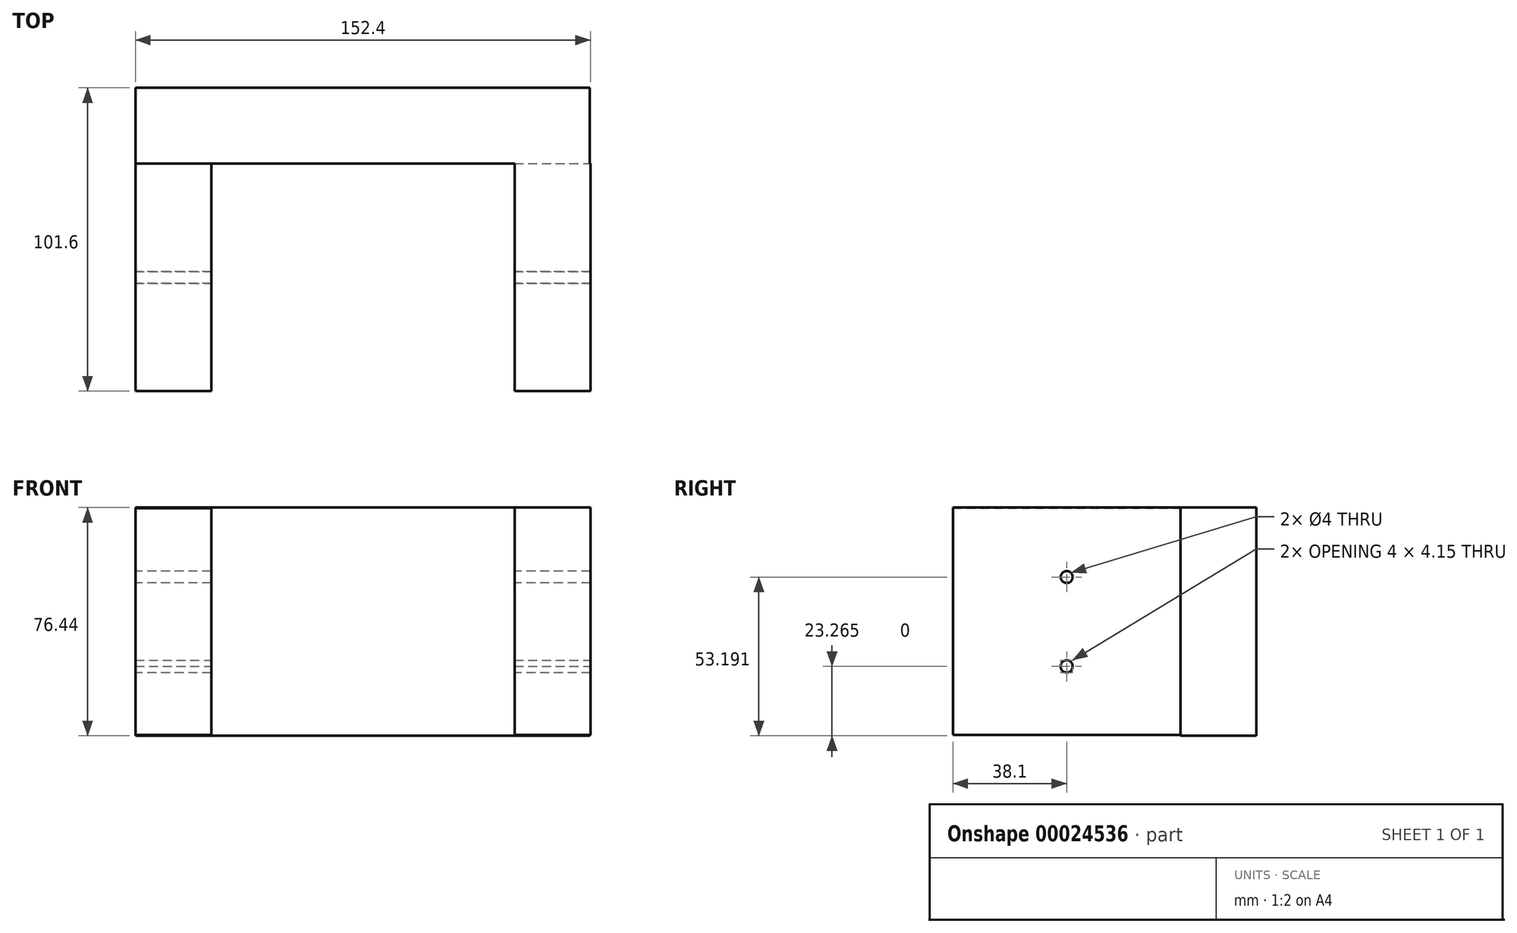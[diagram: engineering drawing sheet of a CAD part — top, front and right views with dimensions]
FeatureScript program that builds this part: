
annotation { "Feature Type Name" : "Feature", "Feature Type Description" : "" }
export const myFeature = defineFeature(function(context is Context, id is Id, definition is map)
    precondition{}
    {
        {
            var Q0;
            Q0=qCreatedBy(makeId("Front.planeOp"),FACE);
            var sketch = newSketch(context, id + "F0", { "sketchPlane" : qUnion([Q0])});
            skLineSegment(sketch, "E0.bottom", {"start": v(0, 0) * mm, "end": v(152.4, 0) * mm});
            skLineSegment(sketch, "E0.top", {"start": v(0, -76.2) * mm, "end": v(152.4, -76.2) * mm});
            skLineSegment(sketch, "E0.left", {"start": v(0, 0) * mm, "end": v(0, -76.2) * mm});
            skLineSegment(sketch, "E0.right", {"start": v(152.4, 0) * mm, "end": v(152.4, -76.2) * mm});
            skLineSegment(sketch, "E1", {"start": v(0, -0.15) * mm, "end": v(25.4, -0.15) * mm});
            skLineSegment(sketch, "E2", {"start": v(152.4, 0.15) * mm, "end": v(127, 0.15) * mm});
            skLineSegment(sketch, "E3", {"start": v(25.4, -0.15) * mm, "end": v(25.4, -76.2) * mm});
            skLineSegment(sketch, "E4", {"start": v(25.4, -76.2) * mm, "end": v(0, -76.2) * mm});
            skLineSegment(sketch, "E5", {"start": v(127, 0.15) * mm, "end": v(127, -76.2) * mm});
            skLineSegment(sketch, "E6", {"start": v(127, -76.2) * mm, "end": v(152.4, -76.2) * mm});
            skSolve(sketch);
        }
        {
            var Q0;
            {var subQ1=sQuery(id+"F0.wireOp",EDGE,"E1");Q0=makeQuery(id+"F0.imprint","IMPRINT",FACE,{"disambiguationData":[TD([[makeQuery(id+"F0.imprint","IMPRINT",EDGE,{"derivedFrom":subQ1}),-1.0]])]});}
            var Q1;
            {var subQ4=sQuery(id+"F0.wireOp",EDGE,"E0.right");Q1=makeQuery(id+"F0.imprint","IMPRINT",FACE,{"disambiguationData":[TD([[makeQuery(id+"F0.imprint","IMPRINT",EDGE,{"derivedFrom":subQ4}),-1.0]])]});}
            extrude(context, id + "F1", {"entities" : qUnion([Q0, Q1]), "depth" : 76.2 * mm});
        }
        {
            var Q0;
            {var subQ1=sQuery(id+"F0.wireOp",EDGE,"E1");Q0=makeQuery(id+"F0.imprint","IMPRINT",FACE,{"disambiguationData":[TD([[makeQuery(id+"F0.imprint","IMPRINT",EDGE,{"derivedFrom":subQ1}),-1.0]])]});}
            var sketch = newSketch(context, id + "F2", { "sketchPlane" : qUnion([Q0])});
            skLineSegment(sketch, "E7.bottom", {"start": v(152.2, 0) * mm, "end": v(0, 0) * mm});
            skLineSegment(sketch, "E7.top", {"start": v(152.2, -76.44) * mm, "end": v(0, -76.44) * mm});
            skLineSegment(sketch, "E7.left", {"start": v(152.2, 0) * mm, "end": v(152.2, -76.44) * mm});
            skLineSegment(sketch, "E7.right", {"start": v(0, 0) * mm, "end": v(0, -76.44) * mm});
            skSolve(sketch);
        }
        {
            var Q0;
            {var subQ3=sQuery(id+"F2.wireOp",EDGE,"E7.bottom");Q0=makeQuery(id+"F2.imprint","IMPRINT",FACE,{"disambiguationData":[TD([[makeQuery(id+"F2.imprint","IMPRINT",EDGE,{"derivedFrom":subQ3}),1.0]])]});}
            extrude(context, id + "F3", {"entities" : qUnion([Q0]), "operationType" : NewBodyOperationType.ADD, "oppositeDirection" : true, "depth" : 25.4 * mm});
        }
        {
            var Q0;
            {var subQ1=sQuery(id+"F0.wireOp",EDGE,"E1");Q0=makeQuery(id+"F0.imprint","IMPRINT",FACE,{"disambiguationData":[TD([[makeQuery(id+"F0.imprint","IMPRINT",EDGE,{"derivedFrom":subQ1}),-1.0]])]});}
            extrude(context, id + "F4", {"entities" : qUnion([Q0]), "operationType" : NewBodyOperationType.ADD, "oppositeDirection" : true, "depth" : 25.4 * mm});
        }
        {
            var Q0;
            {var subQ0=sQuery(id+"F0.wireOp",EDGE,"E0.left");Q0=makeQuery(id+"F4.boolean.opBoolean","MERGE",FACE,{"derivedFrom":[makeQuery(id+"F1.opExtrude","SWEPT_FACE",FACE,{"disambiguationData":[OSD([subQ0])]}),makeQuery(id+"F4.opExtrude","SWEPT_FACE",FACE,{"disambiguationData":[OSD([subQ0])]})]});}
            var sketch = newSketch(context, id + "F5", { "sketchPlane" : qUnion([Q0])});
            skLineSegment(sketch, "E8", {"start": v(38.1, -25.25) * mm, "end": v(38.1, -23.25) * mm});
            skLineSegment(sketch, "E9", {"start": v(38.1, -51.25) * mm, "end": v(38.1, -53.25) * mm});
            skCircle(sketch, "E10", {"center": v(38.1, -23.25) * mm, "radius": 2 * mm});
            skCircle(sketch, "E11", {"center": v(38.1, -53.25) * mm, "radius": 2 * mm});
            skSolve(sketch);
        }
        {
            var Q0;
            Q0=makeQuery(id+"F5.imprint","IMPRINT",FACE,{"disambiguationData":[TD([[makeQuery(id+"F5.imprint","IMPRINT",EDGE,{"derivedFrom":sQuery(id+"F5.wireOp",EDGE,"E10")}),1.0]])]});
            var Q1;
            Q1=makeQuery(id+"F5.imprint","IMPRINT",FACE,{"disambiguationData":[TD([[makeQuery(id+"F5.imprint","IMPRINT",EDGE,{"derivedFrom":sQuery(id+"F5.wireOp",EDGE,"E11")}),1.0]])]});
            extrude(context, id + "F6", {"entities" : qUnion([Q0, Q1]), "operationType" : NewBodyOperationType.REMOVE, "oppositeDirection" : true, "depth" : 254 * mm});
        }
        {
            var Q0;
            Q0=makeQuery(id+"F1.opExtrude","SWEPT_FACE",FACE,{"disambiguationData":[OSD([sQuery(id+"F0.wireOp",EDGE,"E0.right")])]});
            var sketch = newSketch(context, id + "F7", { "sketchPlane" : qUnion([Q0])});
            skLineSegment(sketch, "E12", {"start": v(-38.1, -25.1) * mm, "end": v(-38.1, -23.1) * mm});
            skLineSegment(sketch, "E13", {"start": v(-38.1, -51.1) * mm, "end": v(-38.1, -53.1) * mm});
            skCircle(sketch, "E14", {"center": v(-38.1, -53.1) * mm, "radius": 2 * mm});
            skCircle(sketch, "E15", {"center": v(-38.1, -23.1) * mm, "radius": 2 * mm});
            skSolve(sketch);
        }
        {
            var Q0;
            Q0=makeQuery(id+"F7.imprint","IMPRINT",FACE,{"disambiguationData":[TD([[makeQuery(id+"F7.imprint","IMPRINT",EDGE,{"derivedFrom":sQuery(id+"F7.wireOp",EDGE,"E15")}),1.0]])]});
            var Q1;
            Q1=makeQuery(id+"F7.imprint","IMPRINT",FACE,{"disambiguationData":[TD([[makeQuery(id+"F7.imprint","IMPRINT",EDGE,{"derivedFrom":sQuery(id+"F7.wireOp",EDGE,"E14")}),1.0]])]});
            extrude(context, id + "F8", {"entities" : qUnion([Q0, Q1]), "operationType" : NewBodyOperationType.REMOVE, "endBound" : BoundingType.THROUGH_ALL, "oppositeDirection" : true, "depth" : 25.4 * mm});
        }
    });
